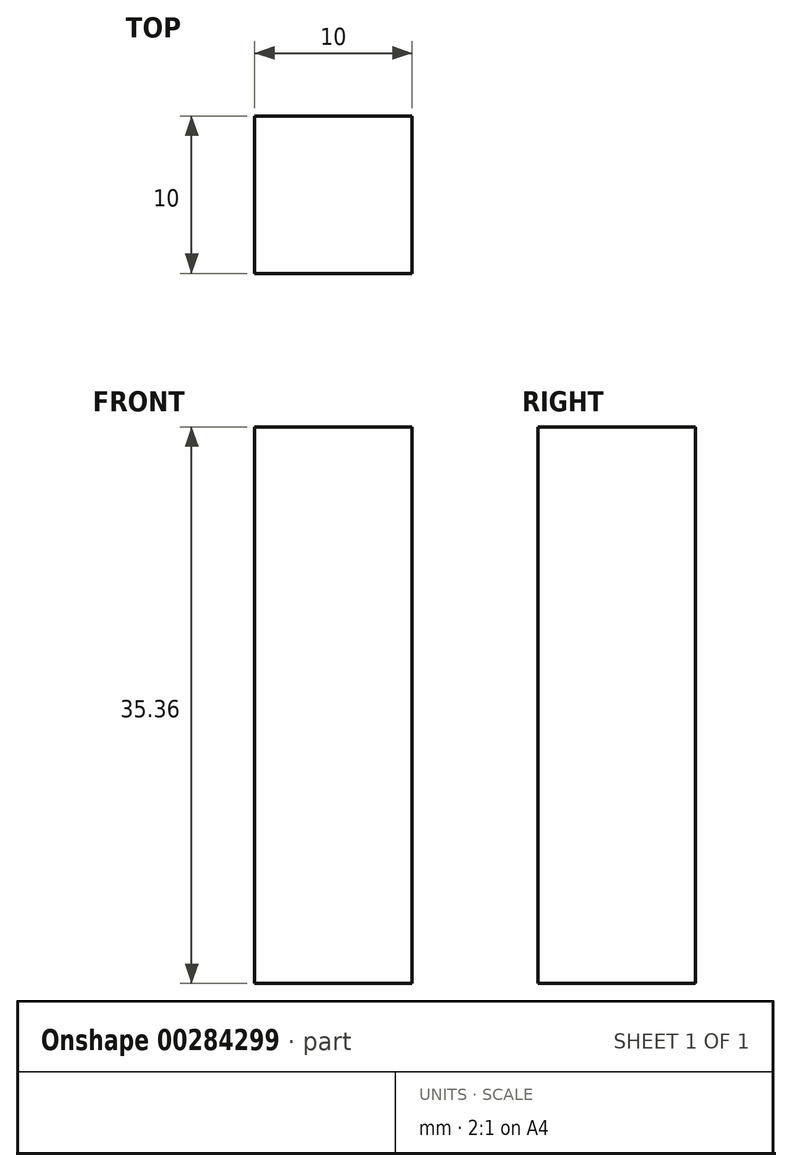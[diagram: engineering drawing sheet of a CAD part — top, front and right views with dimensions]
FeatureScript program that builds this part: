
annotation { "Feature Type Name" : "Feature", "Feature Type Description" : "" }
export const myFeature = defineFeature(function(context is Context, id is Id, definition is map)
    precondition{}
    {
        {
            var Q0;
            Q0=qCreatedBy(makeId("Top.planeOp"),FACE);
            var sketch = newSketch(context, id + "F0", { "sketchPlane" : qUnion([Q0])});
            skLineSegment(sketch, "E0", {"start": v(-50.21, 37.13) * mm, "end": v(-40.21, 37.13) * mm});
            skLineSegment(sketch, "E1", {"start": v(-50.21, 37.13) * mm, "end": v(-50.21, 27.13) * mm});
            skLineSegment(sketch, "E2", {"start": v(-50.21, 27.13) * mm, "end": v(-40.21, 27.13) * mm});
            skLineSegment(sketch, "E3", {"start": v(-40.21, 37.13) * mm, "end": v(-40.21, 27.13) * mm});
            skSolve(sketch);
        }
        {
            var Q0;
            Q0=makeQuery(id+"F0.imprint","IMPRINT",FACE,{"disambiguationData":[TD([[makeQuery(id+"F0.imprint","IMPRINT",EDGE,{"derivedFrom":sQuery(id+"F0.wireOp",EDGE,"E0")}),-1.0]])]});
            extrude(context, id + "F1", {"entities" : qUnion([Q0]), "depth" : 35.36 * mm});
        }
    });
